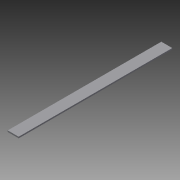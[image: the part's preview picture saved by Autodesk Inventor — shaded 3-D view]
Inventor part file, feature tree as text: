
AUTODESK INVENTOR PART (.ipt)
format: ipt  version: 2015 (Build 190159000, 159)  size: 68,608 bytes
history: native  units: in
note: dims shown in document units (in); Inventor stores cm internally (conversion verified against a paired STEP export)
features: extrude x1, sketch x1
ambient origin geometry x8: Origin, YZ Plane, XZ Plane, XY Plane, X Axis, Y Axis, Z Axis, Center Point
bodies: Solid1 (feature_tree)
feature tree (2):
  extrude  "Extrusion1"  Depth=0.125in
  sketch  "Sketch1"  dims[d0=1.0in d1=0.125in d2=14.0in d3=0.0in]
